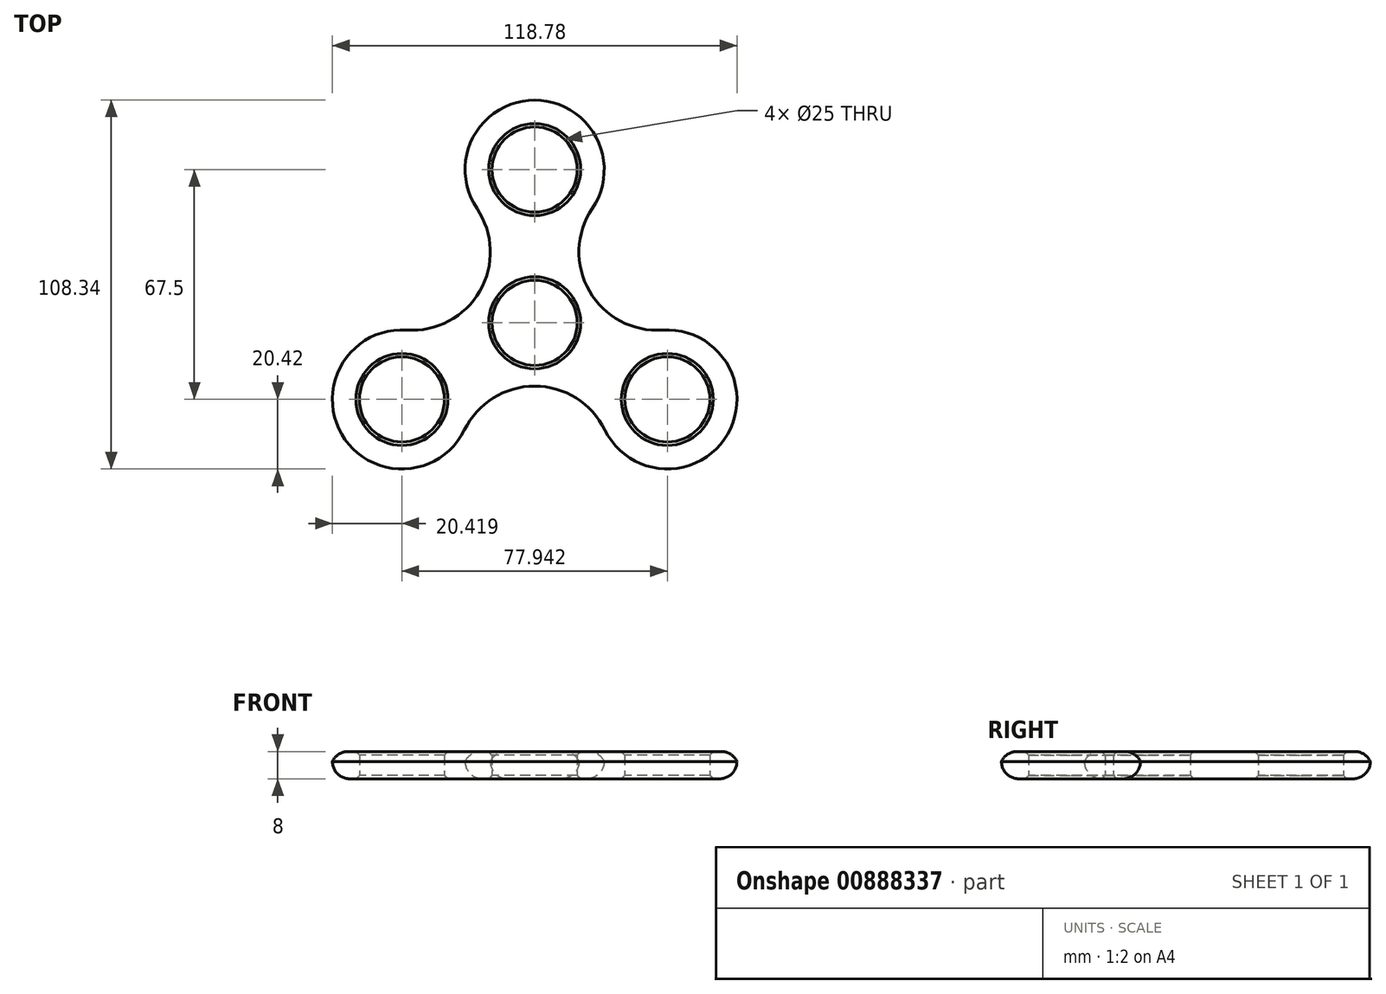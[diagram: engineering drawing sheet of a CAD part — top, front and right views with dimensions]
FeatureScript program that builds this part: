
annotation { "Feature Type Name" : "Feature", "Feature Type Description" : "" }
export const myFeature = defineFeature(function(context is Context, id is Id, definition is map)
    precondition{}
    {
        {
            var Q0;
            Q0=qCreatedBy(makeId("Top.planeOp"),FACE);
            var sketch = newSketch(context, id + "F0", { "sketchPlane" : qUnion([Q0])});
            skCircle(sketch, "E0", {"center": v(0, 0) * mm, "radius": 12.5 * mm});
            skCircle(sketch, "E1", {"center": v(0, 45) * mm, "radius": 12.5 * mm});
            skArc(sketch, "E2", {"start": v(16.94, 33.6) * mm, "mid": v(0, 65.42) * mm, "end": v(-16.94, 33.6) * mm});
            skArc(sketch, "E3.1.0", {"start": v(-37.56, -2.13) * mm, "mid": v(-56.66, -32.71) * mm, "end": v(-20.62, -31.46) * mm});
            skCircle(sketch, "E3.1.1", {"center": v(-38.97, -22.5) * mm, "radius": 12.5 * mm});
            skCircle(sketch, "E3.2.1", {"center": v(38.97, -22.5) * mm, "radius": 12.5 * mm});
            skLineSegment(sketch, "E4", {"start": v(16.94, 33.6) * mm, "end": v(16.94, 33.6) * mm});
            skArc(sketch, "E5.1.0", {"start": v(-37.56, -2.13) * mm, "mid": v(-16.1, 9.3) * mm, "end": v(-16.94, 33.6) * mm});
            skArc(sketch, "E5.2.0", {"start": v(20.62, -31.46) * mm, "mid": v(0, -18.59) * mm, "end": v(-20.62, -31.46) * mm});
            skArc(sketch, "E6", {"start": v(20.62, -31.46) * mm, "mid": v(56.66, -32.71) * mm, "end": v(37.56, -2.13) * mm});
            skArc(sketch, "E7", {"start": v(16.94, 33.6) * mm, "mid": v(16.1, 9.3) * mm, "end": v(37.56, -2.13) * mm});
            skSolve(sketch);
        }
        {
            var Q0;
            Q0 = qSketchRegion(id + "F0", true);
            extrude(context, id + "F1", {"entities" : qUnion([Q0]), "endBound" : BoundingType.SYMMETRIC, "depth" : 8 * mm, "offsetDistance" : 25.4 * mm});
        }
        {
            var Q0;
            Q0=makeQuery(id+"F1.opExtrude","CAP_EDGE",EDGE,{"disambiguationData":[OSD([sQuery(id+"F0.wireOp",EDGE,"E3.1.0")])],"isStart":true});
            var Q1;
            Q1=makeQuery(id+"F1.opExtrude","CAP_EDGE",EDGE,{"disambiguationData":[OSD([sQuery(id+"F0.wireOp",EDGE,"E5.2.0")])],"isStart":true});
            fillet(context, id + "F2", {"entities" : qUnion([Q0, Q1]), "radius" : 5.08 * mm, "tangentPropagation" : true, "allowEdgeOverflow" : false});
        }
        {
            var Q0;
            Q0=makeQuery(id+"F1.opExtrude","CAP_EDGE",EDGE,{"disambiguationData":[OSD([sQuery(id+"F0.wireOp",EDGE,"E3.1.0")])],"isStart":false});
            var Q1;
            Q1=makeQuery(id+"F1.opExtrude","CAP_EDGE",EDGE,{"disambiguationData":[OSD([sQuery(id+"F0.wireOp",EDGE,"E5.1.0")])],"isStart":false});
            fillet(context, id + "F3", {"entities" : qUnion([Q0, Q1]), "radius" : 5.08 * mm, "tangentPropagation" : true, "allowEdgeOverflow" : false});
        }
        {
            var Q0;
            Q0=makeQuery(id+"F1.opExtrude","CAP_EDGE",EDGE,{"disambiguationData":[OSD([sQuery(id+"F0.wireOp",EDGE,"E3.1.1")])],"isStart":false});
            var Q1;
            Q1=makeQuery(id+"F1.opExtrude","CAP_EDGE",EDGE,{"disambiguationData":[OSD([sQuery(id+"F0.wireOp",EDGE,"E1")])],"isStart":false});
            var Q2;
            Q2=makeQuery(id+"F1.opExtrude","CAP_EDGE",EDGE,{"disambiguationData":[OSD([sQuery(id+"F0.wireOp",EDGE,"E3.2.1")])],"isStart":false});
            var Q3;
            Q3=makeQuery(id+"F1.opExtrude","CAP_EDGE",EDGE,{"disambiguationData":[OSD([sQuery(id+"F0.wireOp",EDGE,"E0")])],"isStart":false});
            chamfer(context, id + "F4", {"entities" : qUnion([Q0, Q1, Q2, Q3]), "width" : 1 * mm, "tangentPropagation" : true});
        }
        {
            var Q0;
            Q0=makeQuery(id+"F1.opExtrude","CAP_EDGE",EDGE,{"disambiguationData":[OSD([sQuery(id+"F0.wireOp",EDGE,"E0")])],"isStart":true});
            var Q1;
            Q1=makeQuery(id+"F1.opExtrude","CAP_EDGE",EDGE,{"disambiguationData":[OSD([sQuery(id+"F0.wireOp",EDGE,"E1")])],"isStart":true});
            var Q2;
            Q2=makeQuery(id+"F1.opExtrude","CAP_EDGE",EDGE,{"disambiguationData":[OSD([sQuery(id+"F0.wireOp",EDGE,"E3.1.1")])],"isStart":true});
            var Q3;
            Q3=makeQuery(id+"F1.opExtrude","CAP_EDGE",EDGE,{"disambiguationData":[OSD([sQuery(id+"F0.wireOp",EDGE,"E3.2.1")])],"isStart":true});
            chamfer(context, id + "F5", {"entities" : qUnion([Q0, Q1, Q2, Q3]), "width" : 1 * mm, "tangentPropagation" : true});
        }
    });
